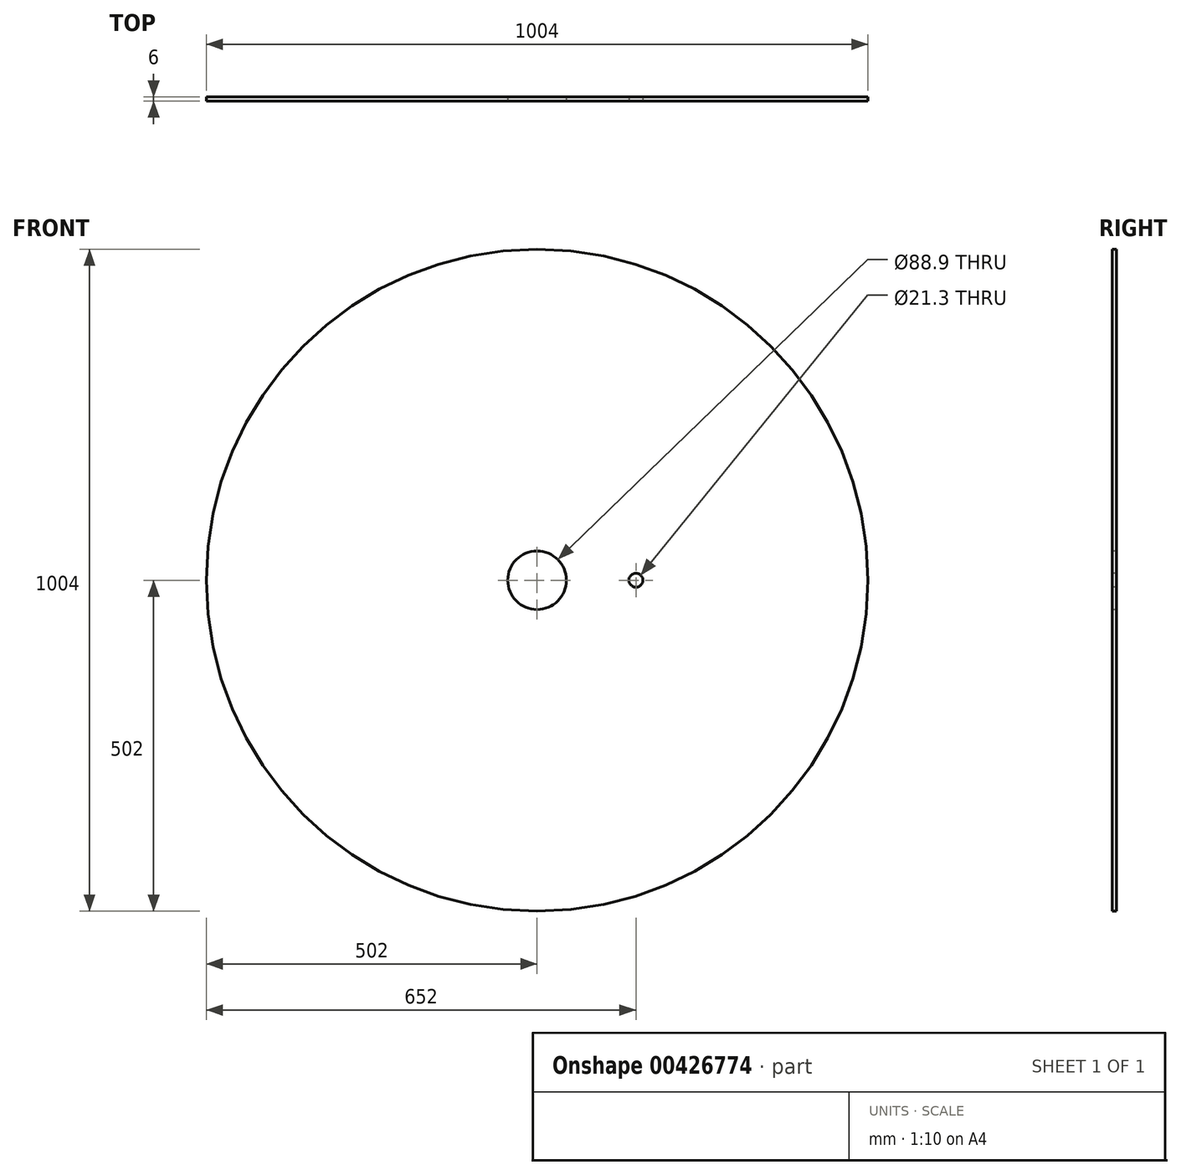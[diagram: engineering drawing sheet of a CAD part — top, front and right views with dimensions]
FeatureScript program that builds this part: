
annotation { "Feature Type Name" : "Feature", "Feature Type Description" : "" }
export const myFeature = defineFeature(function(context is Context, id is Id, definition is map)
    precondition{}
    {
        {
            var Q0;
            Q0=qCreatedBy(makeId("Front.planeOp"),FACE);
            var sketch = newSketch(context, id + "F0", { "sketchPlane" : qUnion([Q0])});
            skCircle(sketch, "E0", {"center": v(0, 0) * mm, "radius": 502 * mm});
            skCircle(sketch, "E1", {"center": v(0, 0) * mm, "radius": 44.45 * mm});
            skCircle(sketch, "E2", {"center": v(150, 0) * mm, "radius": 10.65 * mm});
            skSolve(sketch);
        }
        {
            var Q0;
            Q0=makeQuery(id+"F0.imprint","IMPRINT",FACE,{"disambiguationData":[TD([[makeQuery(id+"F0.imprint","IMPRINT",EDGE,{"derivedFrom":sQuery(id+"F0.wireOp",EDGE,"E0")}),1.0]])]});
            extrude(context, id + "F1", {"entities" : qUnion([Q0]), "oppositeDirection" : true, "depth" : 6 * mm});
        }
    });
